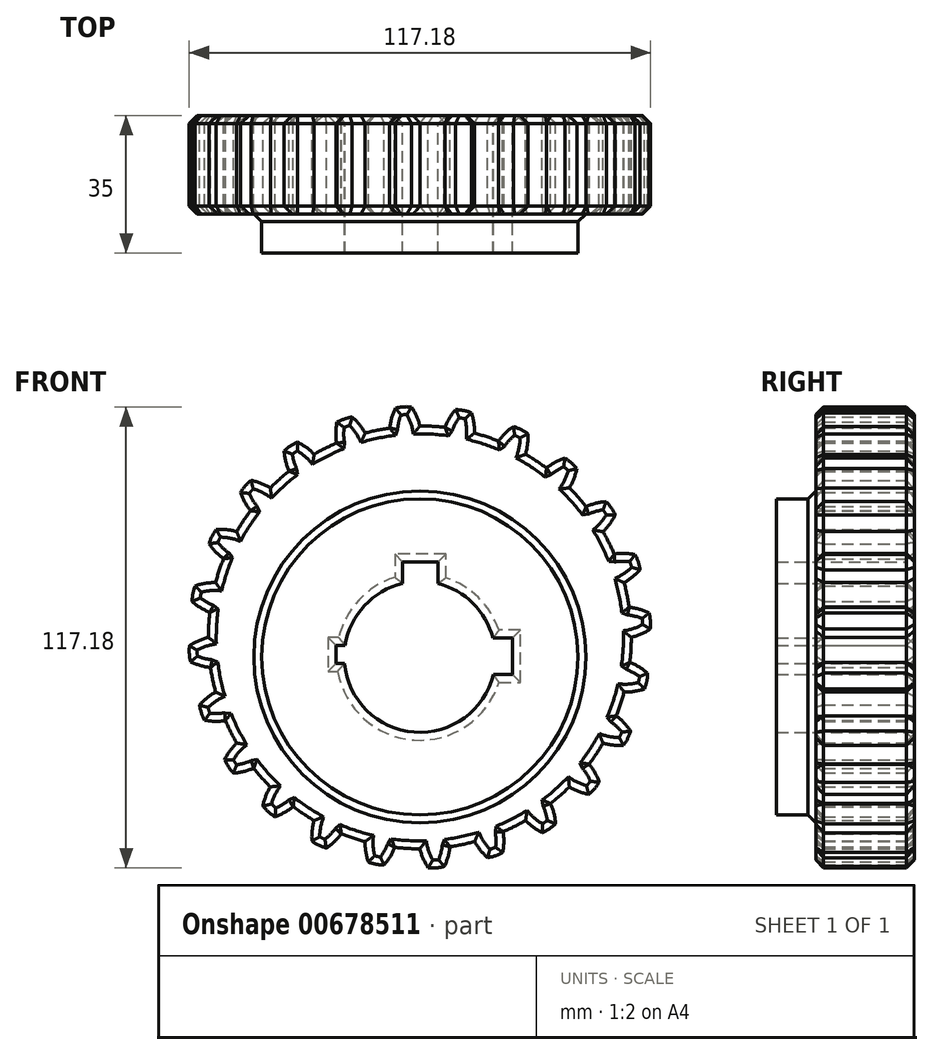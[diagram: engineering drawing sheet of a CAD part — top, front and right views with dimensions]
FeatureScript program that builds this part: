
annotation { "Feature Type Name" : "Feature", "Feature Type Description" : "" }
export const myFeature = defineFeature(function(context is Context, id is Id, definition is map)
    precondition{}
    {
        {
            var Q0;
            Q0=qCreatedBy(makeId("Front.planeOp"),FACE);
            var sketch = newSketch(context, id + "F0", { "sketchPlane" : qUnion([Q0])});
            skCircle(sketch, "E0", {"center": v(0, 4.95) * mm, "radius": 53.72 * mm});
            skCircle(sketch, "E1", {"center": v(0, 0) * mm, "radius": 58.67 * mm, "construction": true});
            skCircle(sketch, "E2", {"center": v(0, 0) * mm, "radius": 63.5 * mm, "construction": true});
            skLineSegment(sketch, "E3", {"start": v(0, 4.95) * mm, "end": v(0, 88.9) * mm, "construction": true});
            skLineSegment(sketch, "E4", {"start": v(0, 0) * mm, "end": v(-5.97, 91.1) * mm, "construction": true});
            skLineSegment(sketch, "E5", {"start": v(0, 58.67) * mm, "end": v(-58.6, 65.36) * mm, "construction": true});
            skLineSegment(sketch, "E6", {"start": v(0, 58.67) * mm, "end": v(-58.6, 44.62) * mm, "construction": true});
            skCircle(sketch, "E7", {"center": v(0, 4.95) * mm, "radius": 52.24 * mm, "construction": true});
            skCircle(sketch, "E8", {"center": v(0, 58.67) * mm, "radius": 14.6 * mm, "construction": true});
            skCircle(sketch, "E9", {"center": v(-14.2, 55.27) * mm, "radius": 14.6 * mm, "construction": true});
            skArc(sketch, "E10", {"start": v(0, 58.67) * mm, "mid": v(-0.85, 61.16) * mm, "end": v(-2.11, 63.46) * mm});
            skLineSegment(sketch, "E11", {"start": v(0, 58.67) * mm, "end": v(0, 58.67) * mm});
            skArc(sketch, "E12.MirrorCS", {"start": v(-7.66, 58.17) * mm, "mid": v(-7.14, 60.75) * mm, "end": v(-6.19, 63.2) * mm});
            skLineSegment(sketch, "E13.MirrorCS", {"start": v(-7.66, 58.17) * mm, "end": v(-7.66, 58.17) * mm});
            skArc(sketch, "E14", {"start": v(-2.11, 63.46) * mm, "mid": v(-4.16, 63.52) * mm, "end": v(-6.19, 63.2) * mm});
            skLineSegment(sketch, "E15", {"start": v(-7.66, 58.17) * mm, "end": v(-7.68, 58.12) * mm});
            skCircle(sketch, "E16", {"center": v(0, 0) * mm, "radius": 19.18 * mm});
            skCircle(sketch, "E17", {"center": v(0, 0) * mm, "radius": 40.16 * mm});
            skLineSegment(sketch, "E18.top", {"start": v(-4.38, 24.1) * mm, "end": v(4.65, 24.1) * mm});
            skLineSegment(sketch, "E18.left", {"start": v(-4.38, 18.67) * mm, "end": v(-4.38, 24.1) * mm});
            skLineSegment(sketch, "E18.right", {"start": v(4.65, 18.75) * mm, "end": v(4.65, 24.1) * mm});
            skLineSegment(sketch, "E19.bottom", {"start": v(18.57, 4.8) * mm, "end": v(23.58, 4.8) * mm});
            skLineSegment(sketch, "E19.top", {"start": v(18.64, -4.5) * mm, "end": v(23.58, -4.5) * mm});
            skLineSegment(sketch, "E19.right", {"start": v(23.58, 4.8) * mm, "end": v(23.58, -4.5) * mm});
            skLineSegment(sketch, "E20.bottom", {"start": v(-19.11, -1.64) * mm, "end": v(-21.34, -1.64) * mm});
            skLineSegment(sketch, "E20.top", {"start": v(-19.18, 2.88) * mm, "end": v(-21.34, 2.88) * mm});
            skLineSegment(sketch, "E20.right", {"start": v(-21.34, -1.64) * mm, "end": v(-21.34, 2.88) * mm});
            skLineSegment(sketch, "E21", {"start": v(4.65, 18.75) * mm, "end": v(4.65, 18.6) * mm});
            skLineSegment(sketch, "E22", {"start": v(-19.18, 2.88) * mm, "end": v(-18.96, 2.88) * mm});
            skSolve(sketch);
        }
        {
            var Q0;
            {var subQ0=sQuery(id+"F0.wireOp",EDGE,"E0");var subQ1=makeQuery(id+"F0.imprint","INTERSECT",VERTEX,{"derivedFrom":[subQ0,sQuery(id+"F0.wireOp",EDGE,"E10")]});Q0=makeQuery(id+"F0.imprint","IMPRINT",FACE,{"disambiguationData":[TD([[makeQuery(id+"F0.imprint","IMPRINT",EDGE,{"disambiguationData":[TD([[subQ1,-1.0]])],"derivedFrom":subQ0}),1.0]])]});}
            var Q1;
            {var subQ0=sQuery(id+"F0.wireOp",EDGE,"E10");Q1=makeQuery(id+"F0.imprint","IMPRINT",FACE,{"disambiguationData":[TD([[makeQuery(id+"F0.imprint","IMPRINT",EDGE,{"derivedFrom":subQ0}),1.0]])]});}
            extrude(context, id + "F1", {"entities" : qUnion([Q0, Q1]), "depth" : 25 * mm, "offsetDistance" : 25 * mm});
        }
        {
            var Q0;
            Q0=makeQuery(id+"F1.opExtrude","SWEPT_BODY",BODY,{"disambiguationData":[OSD([sQuery(id+"F0.wireOp",EDGE,"E0"),sQuery(id+"F0.wireOp",EDGE,"E10"),sQuery(id+"F0.wireOp",EDGE,"E12.MirrorCS"),sQuery(id+"F0.wireOp",EDGE,"E14"),sQuery(id+"F0.wireOp",EDGE,"E15")])]});
            var Q1;
            Q1=makeQuery(id+"F1.opExtrude","SWEPT_FACE",FACE,{"disambiguationData":[OSD([sQuery(id+"F0.wireOp",EDGE,"E0")])]});
            circularPattern(context, id + "F2", {"entities" : qUnion([Q0]), "axis" : qUnion([Q1]), "angle" : 360 * degree, "instanceCount" : 24, "equalSpace" : true});
        }
        {
            var Q0;
            Q0=makeQuery(id+"F0.imprint","IMPRINT",FACE,{"disambiguationData":[TD([[makeQuery(id+"F0.imprint","IMPRINT",EDGE,{"derivedFrom":sQuery(id+"F0.wireOp",EDGE,"E16")}),-1.0]])]});
            extrude(context, id + "F3", {"entities" : qUnion([Q0]), "operationType" : NewBodyOperationType.ADD, "depth" : 35 * mm, "offsetDistance" : 25 * mm});
        }
        {
            var Q0;
            {var subQ0=makeQuery(id+"F1.opExtrude","CAP_FACE",FACE,{"disambiguationData":[OSD([sQuery(id+"F0.wireOp",EDGE,"E0"),sQuery(id+"F0.wireOp",EDGE,"E10"),sQuery(id+"F0.wireOp",EDGE,"E12.MirrorCS"),sQuery(id+"F0.wireOp",EDGE,"E14"),sQuery(id+"F0.wireOp",EDGE,"E15"),sQuery(id+"F0.wireOp",EDGE,"E17")])],"isStart":false});Q0=makeQuery(id+"F3.boolean.opBoolean","MERGE",FACE,{"derivedFrom":[subQ0,makeQuery(id+"F2.opPattern","COPY",FACE,{"derivedFrom":subQ0,"instanceName":"1"}),makeQuery(id+"F2.opPattern","COPY",FACE,{"derivedFrom":subQ0,"instanceName":"2"}),makeQuery(id+"F2.opPattern","COPY",FACE,{"derivedFrom":subQ0,"instanceName":"3"}),makeQuery(id+"F2.opPattern","COPY",FACE,{"derivedFrom":subQ0,"instanceName":"4"}),makeQuery(id+"F2.opPattern","COPY",FACE,{"derivedFrom":subQ0,"instanceName":"5"}),makeQuery(id+"F2.opPattern","COPY",FACE,{"derivedFrom":subQ0,"instanceName":"6"}),makeQuery(id+"F2.opPattern","COPY",FACE,{"derivedFrom":subQ0,"instanceName":"7"}),makeQuery(id+"F2.opPattern","COPY",FACE,{"derivedFrom":subQ0,"instanceName":"8"}),makeQuery(id+"F2.opPattern","COPY",FACE,{"derivedFrom":subQ0,"instanceName":"9"}),makeQuery(id+"F2.opPattern","COPY",FACE,{"derivedFrom":subQ0,"instanceName":"10"}),makeQuery(id+"F2.opPattern","COPY",FACE,{"derivedFrom":subQ0,"instanceName":"11"}),makeQuery(id+"F2.opPattern","COPY",FACE,{"derivedFrom":subQ0,"instanceName":"12"}),makeQuery(id+"F2.opPattern","COPY",FACE,{"derivedFrom":subQ0,"instanceName":"13"}),makeQuery(id+"F2.opPattern","COPY",FACE,{"derivedFrom":subQ0,"instanceName":"14"}),makeQuery(id+"F2.opPattern","COPY",FACE,{"derivedFrom":subQ0,"instanceName":"15"}),makeQuery(id+"F2.opPattern","COPY",FACE,{"derivedFrom":subQ0,"instanceName":"16"}),makeQuery(id+"F2.opPattern","COPY",FACE,{"derivedFrom":subQ0,"instanceName":"17"}),makeQuery(id+"F2.opPattern","COPY",FACE,{"derivedFrom":subQ0,"instanceName":"18"}),makeQuery(id+"F2.opPattern","COPY",FACE,{"derivedFrom":subQ0,"instanceName":"19"}),makeQuery(id+"F2.opPattern","COPY",FACE,{"derivedFrom":subQ0,"instanceName":"20"}),makeQuery(id+"F2.opPattern","COPY",FACE,{"derivedFrom":subQ0,"instanceName":"21"}),makeQuery(id+"F2.opPattern","COPY",FACE,{"derivedFrom":subQ0,"instanceName":"22"}),makeQuery(id+"F2.opPattern","COPY",FACE,{"derivedFrom":subQ0,"instanceName":"23"})]});}
            var Q1;
            {var subQ0=sQuery(id+"F0.wireOp",EDGE,"E17");var subQ1=makeQuery(id+"F1.opExtrude","CAP_FACE",FACE,{"disambiguationData":[OSD([sQuery(id+"F0.wireOp",EDGE,"E0"),sQuery(id+"F0.wireOp",EDGE,"E10"),sQuery(id+"F0.wireOp",EDGE,"E12.MirrorCS"),sQuery(id+"F0.wireOp",EDGE,"E14"),sQuery(id+"F0.wireOp",EDGE,"E15"),subQ0])],"isStart":true});Q1=makeQuery(id+"F3.boolean.opBoolean","MERGE",FACE,{"derivedFrom":[subQ1,makeQuery(id+"F2.opPattern","COPY",FACE,{"derivedFrom":subQ1,"instanceName":"1"}),makeQuery(id+"F2.opPattern","COPY",FACE,{"derivedFrom":subQ1,"instanceName":"2"}),makeQuery(id+"F2.opPattern","COPY",FACE,{"derivedFrom":subQ1,"instanceName":"3"}),makeQuery(id+"F2.opPattern","COPY",FACE,{"derivedFrom":subQ1,"instanceName":"4"}),makeQuery(id+"F2.opPattern","COPY",FACE,{"derivedFrom":subQ1,"instanceName":"5"}),makeQuery(id+"F2.opPattern","COPY",FACE,{"derivedFrom":subQ1,"instanceName":"6"}),makeQuery(id+"F2.opPattern","COPY",FACE,{"derivedFrom":subQ1,"instanceName":"7"}),makeQuery(id+"F2.opPattern","COPY",FACE,{"derivedFrom":subQ1,"instanceName":"8"}),makeQuery(id+"F2.opPattern","COPY",FACE,{"derivedFrom":subQ1,"instanceName":"9"}),makeQuery(id+"F2.opPattern","COPY",FACE,{"derivedFrom":subQ1,"instanceName":"10"}),makeQuery(id+"F2.opPattern","COPY",FACE,{"derivedFrom":subQ1,"instanceName":"11"}),makeQuery(id+"F2.opPattern","COPY",FACE,{"derivedFrom":subQ1,"instanceName":"12"}),makeQuery(id+"F2.opPattern","COPY",FACE,{"derivedFrom":subQ1,"instanceName":"13"}),makeQuery(id+"F2.opPattern","COPY",FACE,{"derivedFrom":subQ1,"instanceName":"14"}),makeQuery(id+"F2.opPattern","COPY",FACE,{"derivedFrom":subQ1,"instanceName":"15"}),makeQuery(id+"F2.opPattern","COPY",FACE,{"derivedFrom":subQ1,"instanceName":"16"}),makeQuery(id+"F2.opPattern","COPY",FACE,{"derivedFrom":subQ1,"instanceName":"17"}),makeQuery(id+"F2.opPattern","COPY",FACE,{"derivedFrom":subQ1,"instanceName":"18"}),makeQuery(id+"F2.opPattern","COPY",FACE,{"derivedFrom":subQ1,"instanceName":"19"}),makeQuery(id+"F2.opPattern","COPY",FACE,{"derivedFrom":subQ1,"instanceName":"20"}),makeQuery(id+"F2.opPattern","COPY",FACE,{"derivedFrom":subQ1,"instanceName":"21"}),makeQuery(id+"F2.opPattern","COPY",FACE,{"derivedFrom":subQ1,"instanceName":"22"}),makeQuery(id+"F2.opPattern","COPY",FACE,{"derivedFrom":subQ1,"instanceName":"23"}),makeQuery(id+"F3.opExtrude","CAP_FACE",FACE,{"disambiguationData":[OSD([sQuery(id+"F0.wireOp",EDGE,"E16"),subQ0,sQuery(id+"F0.wireOp",EDGE,"E18.top"),sQuery(id+"F0.wireOp",EDGE,"E18.left"),sQuery(id+"F0.wireOp",EDGE,"E18.right"),sQuery(id+"F0.wireOp",EDGE,"E19.bottom"),sQuery(id+"F0.wireOp",EDGE,"E19.top"),sQuery(id+"F0.wireOp",EDGE,"E19.right"),sQuery(id+"F0.wireOp",EDGE,"E20.bottom"),sQuery(id+"F0.wireOp",EDGE,"E20.top"),sQuery(id+"F0.wireOp",EDGE,"E20.right"),sQuery(id+"F0.wireOp",EDGE,"yKp54Zqm-Xjpi-HyeE-BbTp-YHzVDFNOd6lc"),sQuery(id+"F0.wireOp",EDGE,"BM7zhOsw-N5jW-aBGP-F87L-TITrQnKRroWP")])],"isStart":true})]});}
            chamfer(context, id + "F4", {"entities" : qUnion([Q0, Q1]), "width" : 2 * mm, "tangentPropagation" : true});
        }
    });
